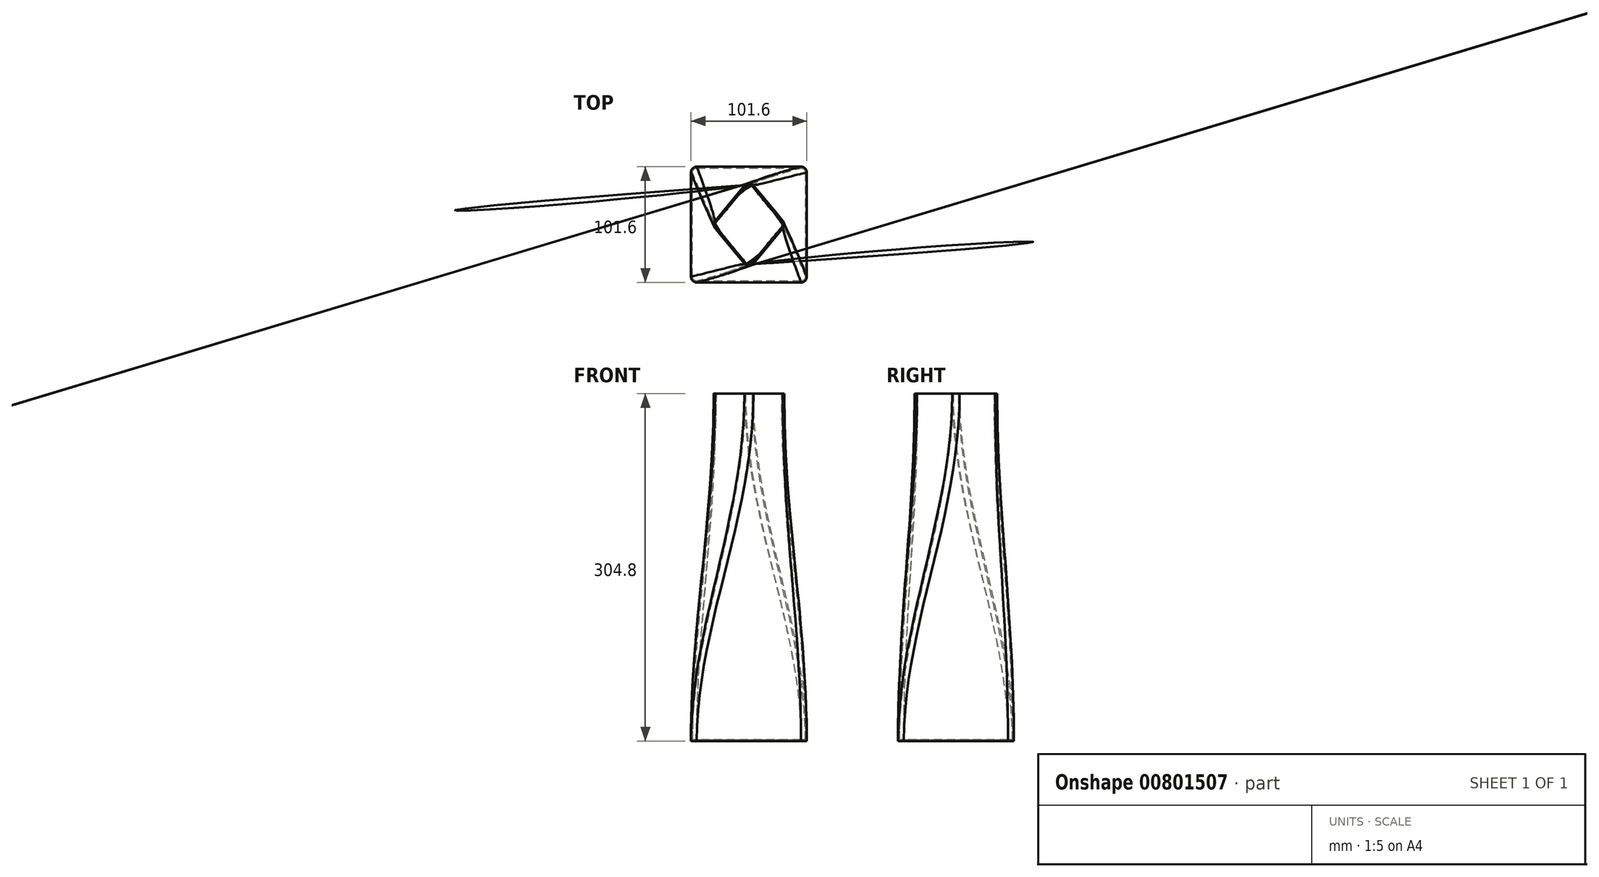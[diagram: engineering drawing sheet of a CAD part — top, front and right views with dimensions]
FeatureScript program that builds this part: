
annotation { "Feature Type Name" : "Feature", "Feature Type Description" : "" }
export const myFeature = defineFeature(function(context is Context, id is Id, definition is map)
    precondition{}
    {
        {
            var Q0;
            Q0=qCreatedBy(makeId("Top.planeOp"),FACE);
            var sketch = newSketch(context, id + "F0", { "sketchPlane" : qUnion([Q0])});
            skLineSegment(sketch, "E0.bottom", {"start": v(50.8, 50.8) * mm, "end": v(-50.8, 50.8) * mm});
            skLineSegment(sketch, "E0.top", {"start": v(50.8, -50.8) * mm, "end": v(-50.8, -50.8) * mm});
            skLineSegment(sketch, "E0.left", {"start": v(50.8, 50.8) * mm, "end": v(50.8, -50.8) * mm});
            skLineSegment(sketch, "E0.right", {"start": v(-50.8, 50.8) * mm, "end": v(-50.8, -50.8) * mm});
            skPoint(sketch, "E0.middle", {"position": v(0, 0) * mm});
            skSolve(sketch);
        }
        {
            var Q0;
            Q0=qCreatedBy(makeId("Top.planeOp"),FACE);
            cPlane(context, id + "F1", {"entities" : qUnion([Q0]), "cplaneType" : CPlaneType.OFFSET, "offset" : 304.8 * mm, "width" : 152.4 * mm, "height" : 152.4 * mm});
        }
        {
            var Q0;
            Q0=qCreatedBy(id+"F1.planeOp",FACE);
            var sketch = newSketch(context, id + "F2", { "sketchPlane" : qUnion([Q0])});
            skPoint(sketch, "E1.middle", {"position": v(0, 0) * mm});
            skLineSegment(sketch, "E2", {"start": v(-32.41, 0) * mm, "end": v(0, 39.12) * mm});
            skLineSegment(sketch, "E3", {"start": v(0, 39.12) * mm, "end": v(32.41, 0) * mm});
            skLineSegment(sketch, "E4", {"start": v(32.41, 0) * mm, "end": v(0, -39.12) * mm});
            skLineSegment(sketch, "E5", {"start": v(0, -39.12) * mm, "end": v(-32.41, 0) * mm});
            skPoint(sketch, "E6.orphan", {"position": v(-32.41, 39.12) * mm});
            skPoint(sketch, "E7.orphan", {"position": v(32.41, 39.12) * mm});
            skPoint(sketch, "E8.orphan", {"position": v(32.41, -39.12) * mm});
            skPoint(sketch, "E1.right.end.orphan", {"position": v(-32.41, -39.12) * mm});
            skSolve(sketch);
        }
        {
            var Q0;
            Q0=makeQuery(id+"F2.imprint","IMPRINT",FACE,{"disambiguationData":[TD([[makeQuery(id+"F2.imprint","IMPRINT",EDGE,{"derivedFrom":sQuery(id+"F2.wireOp",EDGE,"E2")}),-1.0]])]});
            var Q1;
            Q1=makeQuery(id+"F0.imprint","IMPRINT",FACE,{"disambiguationData":[TD([[makeQuery(id+"F0.imprint","IMPRINT",EDGE,{"derivedFrom":sQuery(id+"F0.wireOp",EDGE,"E0.bottom")}),1.0]])]});
            loft(context, id + "F3", {"startCondition" : LoftEndDerivativeType.NORMAL_TO_PROFILE, "startMagnitude" : 1, "endCondition" : LoftEndDerivativeType.NORMAL_TO_PROFILE, "endMagnitude" : 1, "sheetProfilesArray" : [{ "sheetProfileEntities" : qUnion([Q0]) }, { "sheetProfileEntities" : qUnion([Q1]) }]});
        }
        {
            var Q0;
            Q0=makeQuery(id+"F3.opLoft","SWEPT_EDGE",EDGE,{"disambiguationData":[OSD([sQuery(id+"F0.wireOp",EDGE,"E0.top"),sQuery(id+"F0.wireOp",EDGE,"E0.right"),sQuery(id+"F2.wireOp",EDGE,"E2"),sQuery(id+"F2.wireOp",EDGE,"E5")])]});
            var Q1;
            Q1=makeQuery(id+"F3.opLoft","SWEPT_EDGE",EDGE,{"disambiguationData":[OSD([sQuery(id+"F0.wireOp",EDGE,"E0.bottom"),sQuery(id+"F0.wireOp",EDGE,"E0.right"),sQuery(id+"F2.wireOp",EDGE,"E2"),sQuery(id+"F2.wireOp",EDGE,"E3")])]});
            var Q2;
            Q2=makeQuery(id+"F3.opLoft","SWEPT_EDGE",EDGE,{"disambiguationData":[OSD([sQuery(id+"F0.wireOp",EDGE,"E0.top"),sQuery(id+"F0.wireOp",EDGE,"E0.left"),sQuery(id+"F2.wireOp",EDGE,"E4"),sQuery(id+"F2.wireOp",EDGE,"E5")])]});
            var Q3;
            Q3=makeQuery(id+"F3.opLoft","SWEPT_EDGE",EDGE,{"disambiguationData":[OSD([sQuery(id+"F0.wireOp",EDGE,"E0.bottom"),sQuery(id+"F0.wireOp",EDGE,"E0.left"),sQuery(id+"F2.wireOp",EDGE,"E3"),sQuery(id+"F2.wireOp",EDGE,"E4")])]});
            fillet(context, id + "F4", {"entities" : qUnion([Q0, Q1, Q2, Q3]), "radius" : 5.08 * mm, "tangentPropagation" : true, "allowEdgeOverflow" : false});
        }
        {
            var Q0;
            Q0=makeQuery(id+"F3.opLoft","CAP_FACE",FACE,{"disambiguationData":[OSD([makeQuery(id+"F2.imprint","IMPRINT",FACE,{"disambiguationData":[TD([[makeQuery(id+"F2.imprint","IMPRINT",EDGE,{"derivedFrom":sQuery(id+"F2.wireOp",EDGE,"E2")}),-1.0]])]})])],"isStart":true});
            shell(context, id + "F5", {"entities" : qUnion([Q0]), "thickness" : 1.27 * mm});
        }
    });
